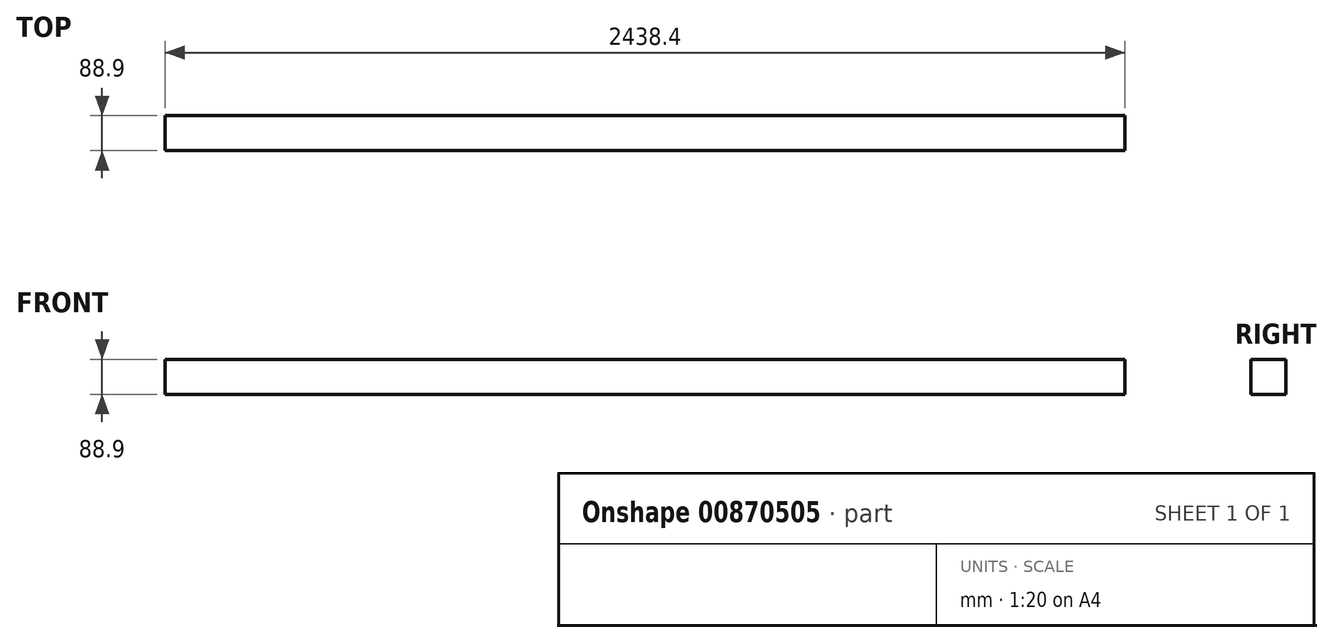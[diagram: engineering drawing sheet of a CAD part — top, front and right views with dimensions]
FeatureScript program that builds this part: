
annotation { "Feature Type Name" : "Feature", "Feature Type Description" : "" }
export const myFeature = defineFeature(function(context is Context, id is Id, definition is map)
    precondition{}
    {
        {
            var Q0;
            Q0=qCreatedBy(makeId("Right.planeOp"),FACE);
            var sketch = newSketch(context, id + "F0", { "sketchPlane" : qUnion([Q0])});
            skLineSegment(sketch, "E0.bottom", {"start": v(0, 0) * mm, "end": v(-88.9, 0) * mm});
            skLineSegment(sketch, "E0.top", {"start": v(0, 88.9) * mm, "end": v(-88.9, 88.9) * mm});
            skLineSegment(sketch, "E0.left", {"start": v(0, 0) * mm, "end": v(0, 88.9) * mm});
            skLineSegment(sketch, "E0.right", {"start": v(-88.9, 0) * mm, "end": v(-88.9, 88.9) * mm});
            skSolve(sketch);
        }
        {
            var Q0;
            Q0 = qSketchRegion(id + "F0", true);
            extrude(context, id + "F1", {"entities" : qUnion([Q0]), "depth" : 2438.4 * mm, "offsetDistance" : 25.4 * mm});
        }
    });
